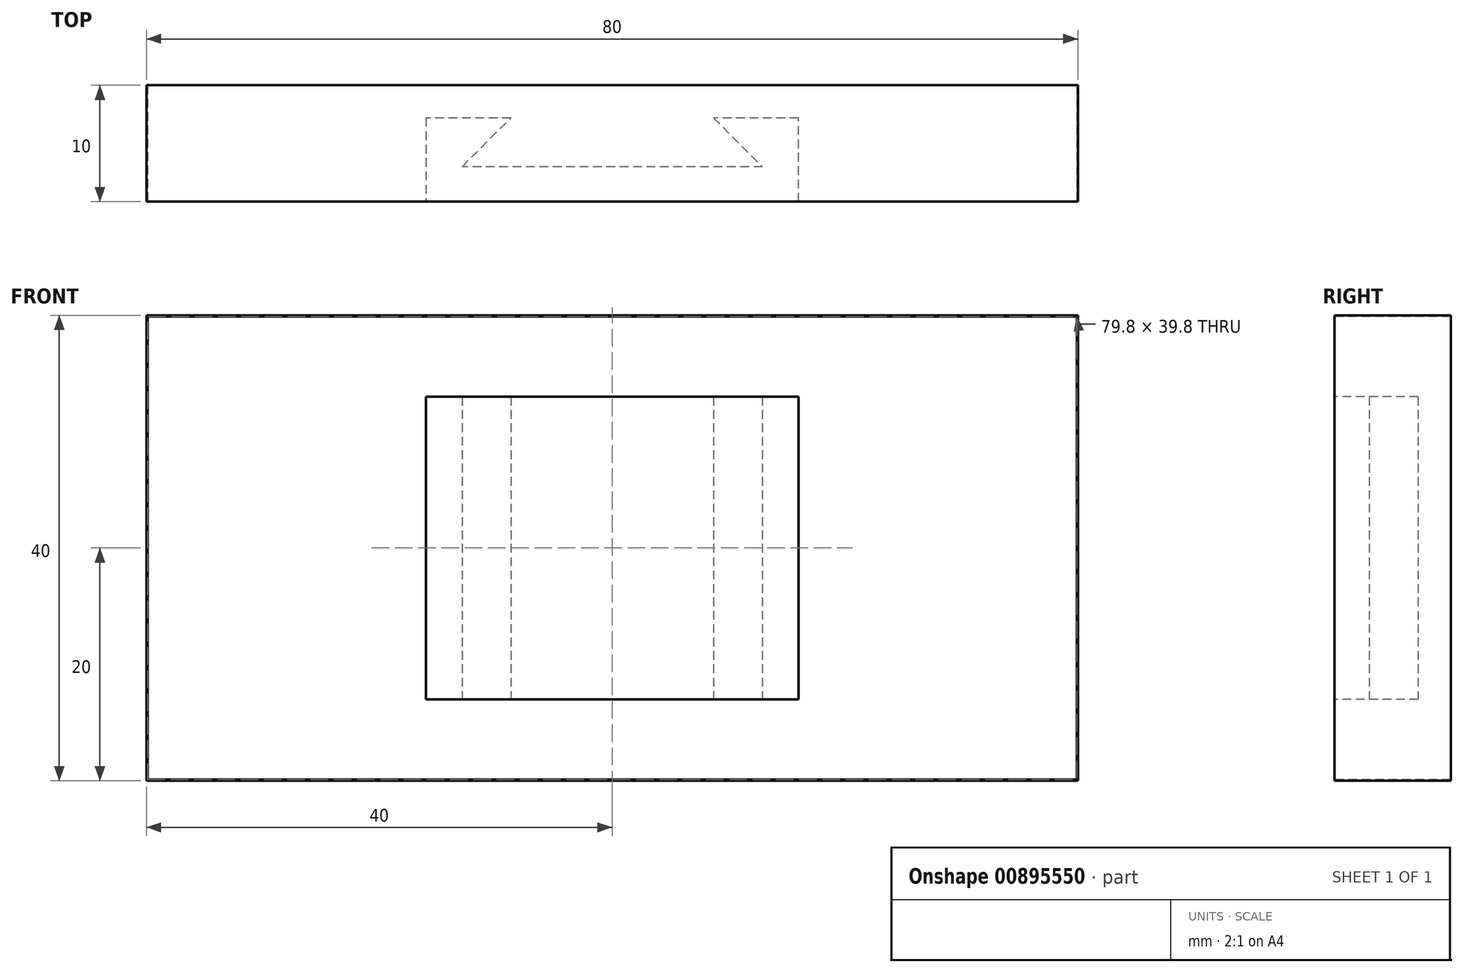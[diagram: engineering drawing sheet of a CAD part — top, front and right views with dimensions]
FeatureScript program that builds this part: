
annotation { "Feature Type Name" : "Feature", "Feature Type Description" : "" }
export const myFeature = defineFeature(function(context is Context, id is Id, definition is map)
    precondition{}
    {
        {
            var Q0;
            Q0=qCreatedBy(makeId("Top.planeOp"),FACE);
            var sketch = newSketch(context, id + "F0", { "sketchPlane" : qUnion([Q0])});
            skLineSegment(sketch, "E0", {"start": v(-16, 0) * mm, "end": v(16, 0) * mm});
            skLineSegment(sketch, "E1", {"start": v(16, 0) * mm, "end": v(16, 7.2) * mm});
            skLineSegment(sketch, "E2", {"start": v(16, 7.2) * mm, "end": v(8.7, 7.2) * mm});
            skLineSegment(sketch, "E3", {"start": v(8.7, 7.2) * mm, "end": v(12.9, 3) * mm});
            skLineSegment(sketch, "E4", {"start": v(12.9, 3) * mm, "end": v(-12.9, 3) * mm});
            skLineSegment(sketch, "E5", {"start": v(-12.9, 3) * mm, "end": v(-8.7, 7.2) * mm});
            skLineSegment(sketch, "E6", {"start": v(-8.7, 7.2) * mm, "end": v(-16, 7.2) * mm});
            skLineSegment(sketch, "E7", {"start": v(-16, 7.2) * mm, "end": v(-16, 0) * mm});
            skSolve(sketch);
        }
        {
            var Q0;
            Q0 = qSketchRegion(id + "F0", true);
            extrude(context, id + "F1", {"entities" : qUnion([Q0]), "depth" : 26 * mm, "offsetDistance" : 25 * mm});
        }
        {
            var Q0;
            {var subQ0=sQuery(id+"F0.wireOp",EDGE,"E1");var subQ7=sQuery(id+"F0.wireOp",EDGE,"E0");Q0=makeQuery(id+"FVxUbPXiXpKRX9N_1.boolean.opBoolean","SPLIT",FACE,{"disambiguationData":[TD([makeQuery(id+"F1.opExtrude","SWEPT_FACE",FACE,{"disambiguationData":[OSD([subQ0])]})])],"derivedFrom":makeQuery(id+"F1.opExtrude","SWEPT_FACE",FACE,{"disambiguationData":[OSD([subQ7])]})});}
            var sketch = newSketch(context, id + "F2", { "sketchPlane" : qUnion([Q0])});
            skLineSegment(sketch, "E8.bottom", {"start": v(-40, 33) * mm, "end": v(40, 33) * mm});
            skLineSegment(sketch, "E8.top", {"start": v(-40, -7) * mm, "end": v(40, -7) * mm});
            skLineSegment(sketch, "E8.left", {"start": v(-40, 33) * mm, "end": v(-40, -7) * mm});
            skLineSegment(sketch, "E8.right", {"start": v(40, 33) * mm, "end": v(40, -7) * mm});
            skLineSegment(sketch, "E9.bottom", {"start": v(-39.9, 32.9) * mm, "end": v(39.9, 32.9) * mm});
            skLineSegment(sketch, "E9.top", {"start": v(-39.9, -6.9) * mm, "end": v(39.9, -6.9) * mm});
            skLineSegment(sketch, "E9.left", {"start": v(-39.9, 32.9) * mm, "end": v(-39.9, -6.9) * mm});
            skLineSegment(sketch, "E9.right", {"start": v(39.9, 32.9) * mm, "end": v(39.9, -6.9) * mm});
            skSolve(sketch);
        }
        {
            var Q0;
            Q0 = qSketchRegion(id + "F2", true);
            extrude(context, id + "F3", {"entities" : qUnion([Q0]), "oppositeDirection" : true, "depth" : 10 * mm, "offsetDistance" : 25 * mm});
        }
    });
